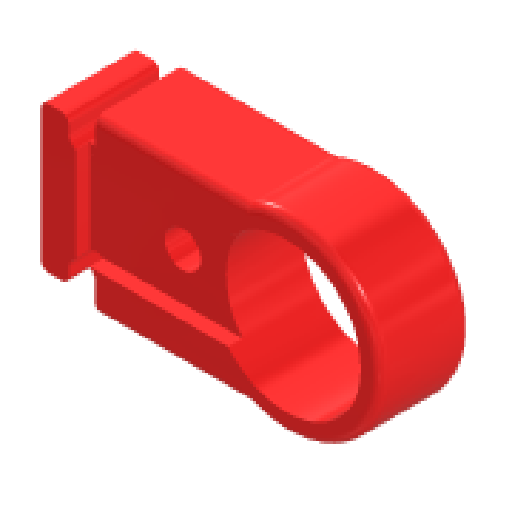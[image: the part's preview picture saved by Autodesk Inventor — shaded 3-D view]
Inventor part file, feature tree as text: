
AUTODESK INVENTOR PART (.ipt)
format: ipt  version: 2023 (Build 270158000, 158)  size: 215,552 bytes
history: native  units: in
note: dims shown in document units (in); Inventor stores cm internally (conversion verified against a paired STEP export)
features: reference x15, extrude x5, sketch x5, other x4, fillet x1
ambient origin geometry x8: Origin, YZ Plane, XZ Plane, XY Plane, X Axis, Y Axis, Z Axis, Center Point
bodies: Solid1 (feature_tree)
feature tree (30):
  extrude  "Extrusion1"  Depth=0.0079in
  extrude  "Extrusion2"  Depth=0.3937in
  extrude  "Extrusion3"  Depth=0.1575in
  extrude  "Extrusion4"  Depth=0.1575in
  extrude  "Extrusion5"  Depth=0.0394in TaperAngle=0.0deg
  fillet  "Fillet2"  Radius=0.315in
  sketch  "Sketch1"  dims[d0=0.0079in d1=0.0079in]
  reference  "Reference1"
  reference  "Reference2"
  reference  "Reference3"
  reference  "Reference4"
  reference  "Reference5"
  reference  "Reference6"
  reference  "Reference7"
  reference  "Reference8"
  reference  "Reference9"
  reference  "Reference10"
  reference  "Reference11"
  reference  "Reference12"
  sketch  "Sketch2"  dims[d2=0.3937in d3=0.0in d4=0.0079in]
  reference  "Reference13"
  sketch  "Sketch3"  dims[d5=0.063in d6=0.0in d7=0.1575in]
  sketch  "Sketch4"  dims[d8=0.315in d9=0.0in d10=0.1575in]
  sketch  "Sketch5"  dims[d11=0.1969in d12=0.315in d13=0.0in d15=0.315in d16=0.0in d17=0.0394in]
  reference  "Reference14"
  reference  "Reference15"
  other  "<userpath>\Documents\Github\Acoustifly\CAD\1_Col_Print\Assembly.iam"
  other  "Assembly.iam"
  other  "VerticalProfile:1"
  other  "TransducerPCB_Acoustifly:1"
